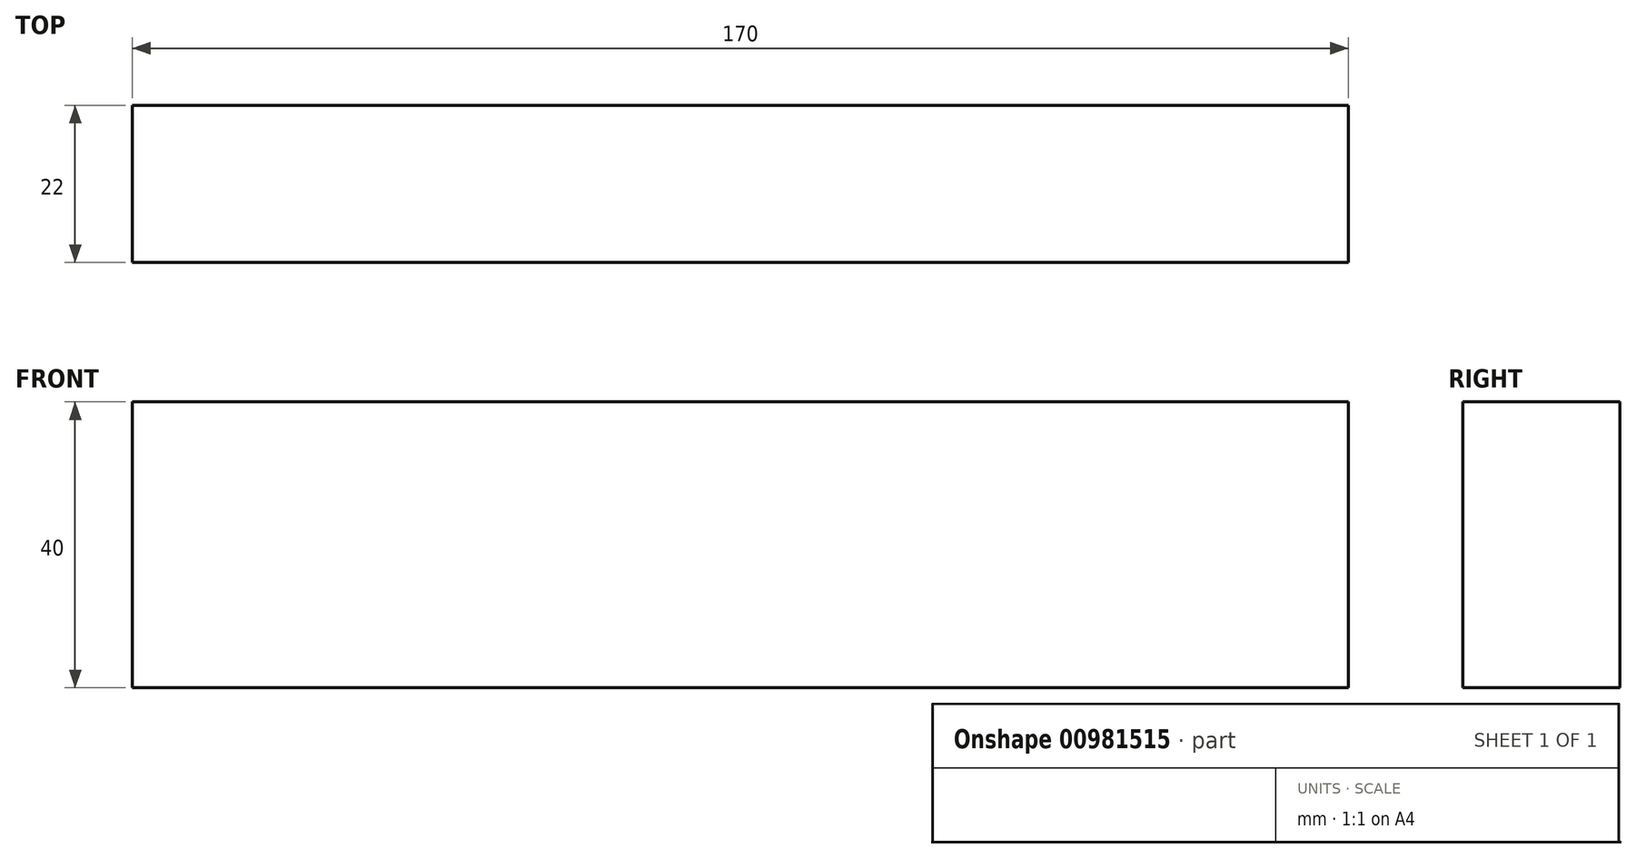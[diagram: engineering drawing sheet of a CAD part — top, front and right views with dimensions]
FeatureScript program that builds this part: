
annotation { "Feature Type Name" : "Feature", "Feature Type Description" : "" }
export const myFeature = defineFeature(function(context is Context, id is Id, definition is map)
    precondition{}
    {
        {
            var Q0;
            Q0=qCreatedBy(makeId("Right.planeOp"),FACE);
            var sketch = newSketch(context, id + "F0", { "sketchPlane" : qUnion([Q0])});
            skLineSegment(sketch, "E0.bottom", {"start": v(-30.65, 67.88) * mm, "end": v(-8.65, 67.88) * mm});
            skLineSegment(sketch, "E0.top", {"start": v(-30.65, 27.88) * mm, "end": v(-8.65, 27.88) * mm});
            skLineSegment(sketch, "E0.left", {"start": v(-30.65, 67.88) * mm, "end": v(-30.65, 27.88) * mm});
            skLineSegment(sketch, "E0.right", {"start": v(-8.65, 67.88) * mm, "end": v(-8.65, 27.88) * mm});
            skLineSegment(sketch, "E1.bottom", {"start": v(-30.65, 63.88) * mm, "end": v(-20.65, 63.88) * mm});
            skLineSegment(sketch, "E1.top", {"start": v(-30.65, 55.88) * mm, "end": v(-20.65, 55.88) * mm});
            skLineSegment(sketch, "E1.left", {"start": v(-30.65, 63.88) * mm, "end": v(-30.65, 55.88) * mm});
            skLineSegment(sketch, "E1.right", {"start": v(-20.65, 63.88) * mm, "end": v(-20.65, 55.88) * mm});
            skSolve(sketch);
        }
        {
            var Q0;
            Q0=makeQuery(id+"F0.imprint","IMPRINT",FACE,{"disambiguationData":[TD([[makeQuery(id+"F0.imprint","IMPRINT",EDGE,{"derivedFrom":sQuery(id+"F0.wireOp",EDGE,"E1.bottom")}),-1.0]])]});
            var Q1;
            {var subQ4=sQuery(id+"F0.wireOp",EDGE,"E0.bottom");Q1=makeQuery(id+"F0.imprint","IMPRINT",FACE,{"disambiguationData":[TD([[makeQuery(id+"F0.imprint","IMPRINT",EDGE,{"derivedFrom":subQ4}),-1.0]])]});}
            extrude(context, id + "F1", {"entities" : qUnion([Q0, Q1]), "depth" : 170 * mm, "offsetDistance" : 25 * mm});
        }
    });
